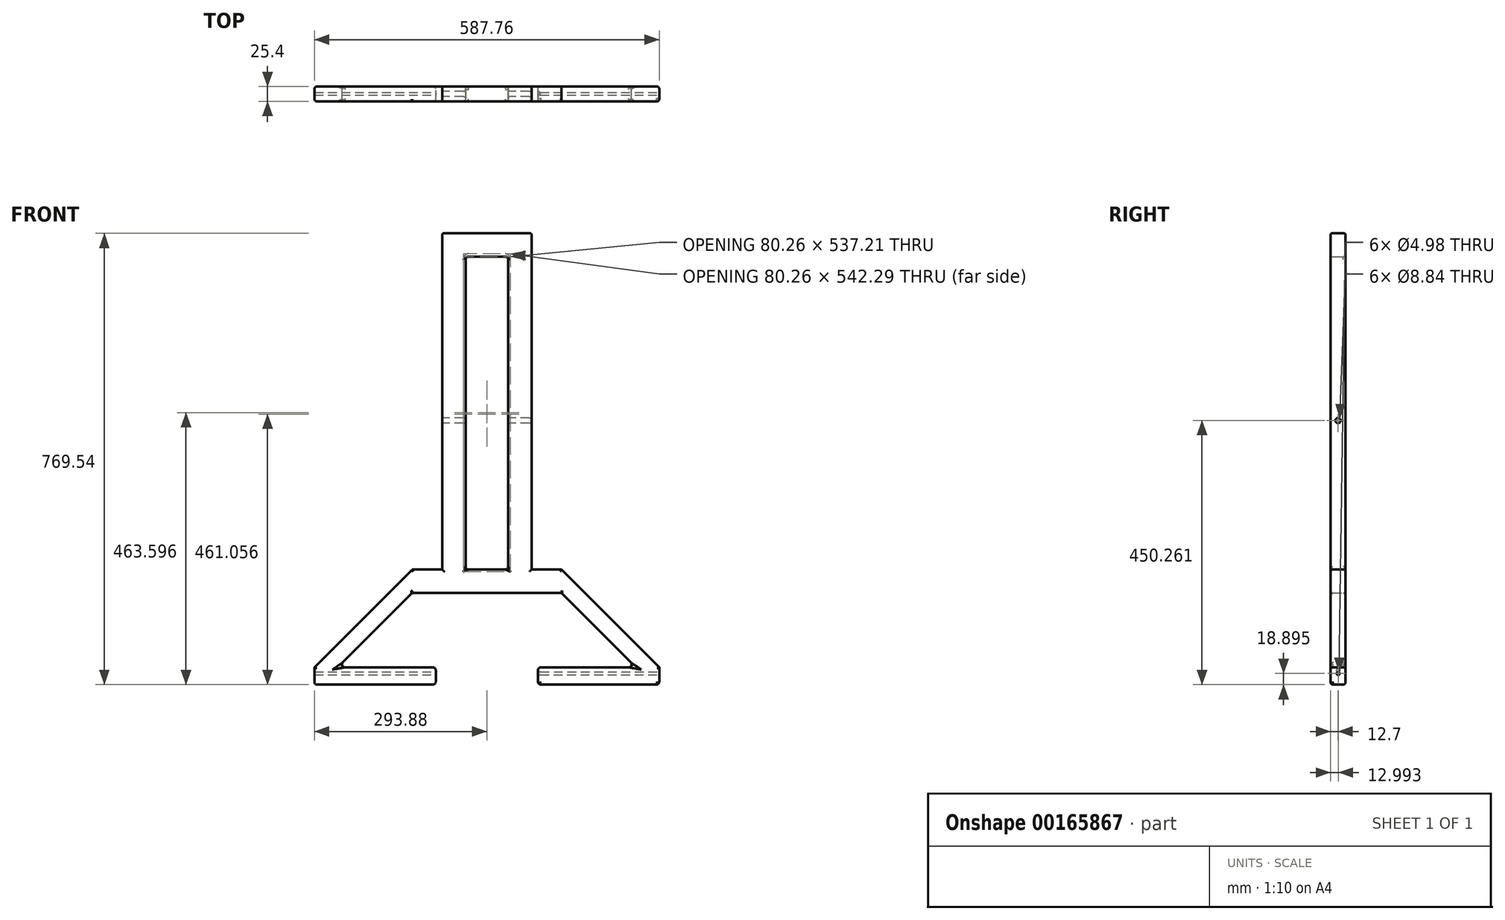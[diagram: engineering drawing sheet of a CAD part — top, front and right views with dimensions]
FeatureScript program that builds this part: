
annotation { "Feature Type Name" : "Feature", "Feature Type Description" : "" }
export const myFeature = defineFeature(function(context is Context, id is Id, definition is map)
    precondition{}
    {
        {
            var Q0;
            Q0=qCreatedBy(makeId("Front.planeOp"),FACE);
            var sketch = newSketch(context, id + "F0", { "sketchPlane" : qUnion([Q0])});
            skLineSegment(sketch, "E0.bottom", {"start": v(76.2, 19.94) * mm, "end": v(-76.2, 19.94) * mm});
            skLineSegment(sketch, "E0.top", {"start": v(76.2, -19.94) * mm, "end": v(-76.2, -19.94) * mm});
            skLineSegment(sketch, "E0.left", {"start": v(76.2, 19.94) * mm, "end": v(76.2, -19.94) * mm});
            skLineSegment(sketch, "E0.right", {"start": v(-76.2, 19.94) * mm, "end": v(-76.2, -19.94) * mm});
            skPoint(sketch, "E0.middle", {"position": v(0, 0) * mm});
            skLineSegment(sketch, "E1", {"start": v(-76.2, 19.94) * mm, "end": v(-36.32, 19.94) * mm});
            skLineSegment(sketch, "E2", {"start": v(-36.32, 19.94) * mm, "end": v(-36.32, -19.94) * mm});
            skLineSegment(sketch, "E3.MirrorCS", {"start": v(36.32, 19.94) * mm, "end": v(36.32, -19.94) * mm});
            skLineSegment(sketch, "E4", {"start": v(-76.2, -19.94) * mm, "end": v(-76.2, -553.34) * mm});
            skLineSegment(sketch, "E5", {"start": v(-36.32, -19.94) * mm, "end": v(-36.32, -553.34) * mm});
            skLineSegment(sketch, "E6", {"start": v(0, 0) * mm, "end": v(0, -73.17) * mm});
            skPoint(sketch, "E6.endSnap0", {"position": v(0, -19.94) * mm});
            skLineSegment(sketch, "E7.MirrorCS", {"start": v(36.32, -19.94) * mm, "end": v(36.32, -553.34) * mm});
            skLineSegment(sketch, "E8.MirrorCS", {"start": v(76.2, -19.94) * mm, "end": v(76.2, -553.34) * mm});
            skLineSegment(sketch, "E9", {"start": v(76.2, -553.34) * mm, "end": v(36.32, -553.34) * mm});
            skLineSegment(sketch, "E10", {"start": v(-36.32, -553.34) * mm, "end": v(-76.2, -553.34) * mm});
            skLineSegment(sketch, "E11", {"start": v(76.2, -553.34) * mm, "end": v(127, -553.34) * mm});
            skLineSegment(sketch, "E12", {"start": v(127, -553.34) * mm, "end": v(127, -593.22) * mm});
            skLineSegment(sketch, "E13", {"start": v(-76.2, -553.34) * mm, "end": v(-127, -553.34) * mm});
            skLineSegment(sketch, "E14", {"start": v(-127, -553.34) * mm, "end": v(-127, -593.22) * mm});
            skLineSegment(sketch, "E15", {"start": v(-127, -593.22) * mm, "end": v(127, -593.22) * mm});
            skLineSegment(sketch, "E16", {"start": v(36.32, -553.34) * mm, "end": v(-36.32, -553.34) * mm});
            skLineSegment(sketch, "E17", {"start": v(-127, -593.22) * mm, "end": v(-87.12, -593.22) * mm});
            skLineSegment(sketch, "E18", {"start": v(127, -593.22) * mm, "end": v(87.12, -593.22) * mm});
            skLineSegment(sketch, "E19", {"start": v(-127, -593.22) * mm, "end": v(-127, -720.22) * mm});
            skLineSegment(sketch, "E20", {"start": v(-87.12, -593.22) * mm, "end": v(-87.12, -720.22) * mm});
            skLineSegment(sketch, "E21", {"start": v(127, -593.22) * mm, "end": v(127, -720.22) * mm});
            skLineSegment(sketch, "E22", {"start": v(87.12, -593.22) * mm, "end": v(87.12, -720.22) * mm});
            skLineSegment(sketch, "E23", {"start": v(-127, -720.22) * mm, "end": v(-87.12, -720.22) * mm});
            skLineSegment(sketch, "E24", {"start": v(87.12, -720.22) * mm, "end": v(127, -720.22) * mm});
            skLineSegment(sketch, "E25", {"start": v(-127, -720.22) * mm, "end": v(-254, -720.22) * mm});
            skLineSegment(sketch, "E26", {"start": v(127, -720.22) * mm, "end": v(254, -720.22) * mm});
            skLineSegment(sketch, "E27", {"start": v(-127, -593.22) * mm, "end": v(-254, -720.22) * mm});
            skPoint(sketch, "E28.startSnap0", {"position": v(0, -593.22) * mm});
            skLineSegment(sketch, "E29.MirrorCS", {"start": v(127, -593.22) * mm, "end": v(254, -720.22) * mm});
            skLineSegment(sketch, "E30", {"start": v(-254, -720.22) * mm, "end": v(-293.88, -720.22) * mm});
            skLineSegment(sketch, "E31", {"start": v(-127, -553.34) * mm, "end": v(-293.88, -720.22) * mm});
            skLineSegment(sketch, "E32.MirrorCS", {"start": v(254, -720.22) * mm, "end": v(293.88, -720.22) * mm});
            skLineSegment(sketch, "E33.MirrorCS", {"start": v(127, -553.34) * mm, "end": v(293.88, -720.22) * mm});
            skLineSegment(sketch, "E34", {"start": v(-293.88, -720.22) * mm, "end": v(-293.88, -749.6) * mm});
            skLineSegment(sketch, "E35", {"start": v(-293.88, -749.6) * mm, "end": v(-87.12, -749.6) * mm});
            skLineSegment(sketch, "E36", {"start": v(-87.12, -720.22) * mm, "end": v(-87.12, -749.6) * mm});
            skLineSegment(sketch, "E37.MirrorCS", {"start": v(293.88, -720.22) * mm, "end": v(293.88, -749.6) * mm});
            skLineSegment(sketch, "E38.MirrorCS", {"start": v(293.88, -749.6) * mm, "end": v(87.12, -749.6) * mm});
            skLineSegment(sketch, "E39.MirrorCS", {"start": v(87.12, -720.22) * mm, "end": v(87.12, -749.6) * mm});
            skSolve(sketch);
        }
        {
            var Q0;
            {var subQ0=sQuery(id+"F0.wireOp",EDGE,"E0.left");Q0=makeQuery(id+"F0.imprint","IMPRINT",FACE,{"disambiguationData":[TD([[makeQuery(id+"F0.imprint","IMPRINT",EDGE,{"derivedFrom":subQ0}),-1.0]])]});}
            var Q1;
            {var subQ0=sQuery(id+"F0.wireOp",EDGE,"E0.right");Q1=makeQuery(id+"F0.imprint","IMPRINT",FACE,{"disambiguationData":[TD([[makeQuery(id+"F0.imprint","IMPRINT",EDGE,{"derivedFrom":subQ0}),1.0]])]});}
            var Q2;
            {var subQ0=sQuery(id+"F0.wireOp",EDGE,"E2");Q2=makeQuery(id+"F0.imprint","IMPRINT",FACE,{"disambiguationData":[TD([[makeQuery(id+"F0.imprint","IMPRINT",EDGE,{"derivedFrom":subQ0}),1.0]])]});}
            var Q3;
            Q3=makeQuery(id+"F0.imprint","IMPRINT",FACE,{"disambiguationData":[TD([[makeQuery(id+"F0.imprint","IMPRINT",EDGE,{"derivedFrom":sQuery(id+"F0.wireOp",EDGE,"E12")}),1.0]])]});
            var Q4;
            Q4=makeQuery(id+"F0.imprint","IMPRINT",FACE,{"disambiguationData":[TD([[makeQuery(id+"F0.imprint","IMPRINT",EDGE,{"derivedFrom":sQuery(id+"F0.wireOp",EDGE,"E14")}),-1.0]])]});
            var Q5;
            Q5=makeQuery(id+"F0.imprint","IMPRINT",FACE,{"disambiguationData":[TD([[makeQuery(id+"F0.imprint","IMPRINT",EDGE,{"derivedFrom":sQuery(id+"F0.wireOp",EDGE,"E17")}),-1.0]])]});
            var Q6;
            Q6=makeQuery(id+"F0.imprint","IMPRINT",FACE,{"disambiguationData":[TD([[makeQuery(id+"F0.imprint","IMPRINT",EDGE,{"derivedFrom":sQuery(id+"F0.wireOp",EDGE,"E18")}),1.0]])]});
            var Q7;
            Q7=makeQuery(id+"F0.imprint","IMPRINT",FACE,{"disambiguationData":[TD([[makeQuery(id+"F0.imprint","IMPRINT",EDGE,{"derivedFrom":sQuery(id+"F0.wireOp",EDGE,"E23")}),-1.0]])]});
            var Q8;
            Q8=makeQuery(id+"F0.imprint","IMPRINT",FACE,{"disambiguationData":[TD([[makeQuery(id+"F0.imprint","IMPRINT",EDGE,{"derivedFrom":sQuery(id+"F0.wireOp",EDGE,"E9")}),1.0]])]});
            var Q9;
            Q9=makeQuery(id+"F0.imprint","IMPRINT",FACE,{"disambiguationData":[TD([[makeQuery(id+"F0.imprint","IMPRINT",EDGE,{"derivedFrom":sQuery(id+"F0.wireOp",EDGE,"E24")}),-1.0]])]});
            var Q10;
            {var subQ2=sQuery(id+"F0.wireOp",EDGE,"E7.MirrorCS");Q10=makeQuery(id+"F0.imprint","IMPRINT",FACE,{"disambiguationData":[TD([[makeQuery(id+"F0.imprint","IMPRINT",EDGE,{"derivedFrom":subQ2}),1.0]])]});}
            var Q11;
            {var subQ0=sQuery(id+"F0.wireOp",EDGE,"E4");Q11=makeQuery(id+"F0.imprint","IMPRINT",FACE,{"disambiguationData":[TD([[makeQuery(id+"F0.imprint","IMPRINT",EDGE,{"derivedFrom":subQ0}),1.0]])]});}
            extrude(context, id + "F1", {"entities" : qUnion([Q0, Q1, Q2, Q3, Q4, Q5, Q6, Q7, Q8, Q9, Q10, Q11]), "depth" : 25.4 * mm});
        }
        {
            var Q0;
            Q0=makeQuery(id+"F1.opExtrude","CAP_EDGE",EDGE,{"disambiguationData":[OSD([sQuery(id+"F0.wireOp",EDGE,"E0.right"),sQuery(id+"F0.wireOp",EDGE,"E4")])],"isStart":false});
            var Q1;
            Q1=makeQuery(id+"F1.opExtrude","CAP_EDGE",EDGE,{"disambiguationData":[OSD([sQuery(id+"F0.wireOp",EDGE,"E13")])],"isStart":false});
            var Q2;
            Q2=makeQuery(id+"F1.opExtrude","CAP_EDGE",EDGE,{"disambiguationData":[OSD([sQuery(id+"F0.wireOp",EDGE,"E34")])],"isStart":false});
            var Q3;
            Q3=makeQuery(id+"F1.opExtrude","CAP_EDGE",EDGE,{"disambiguationData":[OSD([sQuery(id+"F0.wireOp",EDGE,"E35")])],"isStart":false});
            var Q4;
            Q4=makeQuery(id+"F1.opExtrude","CAP_EDGE",EDGE,{"disambiguationData":[OSD([sQuery(id+"F0.wireOp",EDGE,"E20"),sQuery(id+"F0.wireOp",EDGE,"E36")])],"isStart":false});
            var Q5;
            Q5=makeQuery(id+"F1.opExtrude","CAP_EDGE",EDGE,{"disambiguationData":[OSD([sQuery(id+"F0.wireOp",EDGE,"E31")])],"isStart":false});
            var Q6;
            Q6=makeQuery(id+"F1.opExtrude","CAP_EDGE",EDGE,{"disambiguationData":[OSD([sQuery(id+"F0.wireOp",EDGE,"E21")])],"isStart":false});
            var Q7;
            Q7=makeQuery(id+"F1.opExtrude","CAP_EDGE",EDGE,{"disambiguationData":[OSD([sQuery(id+"F0.wireOp",EDGE,"E29.MirrorCS")])],"isStart":false});
            var Q8;
            Q8=makeQuery(id+"F1.opExtrude","CAP_EDGE",EDGE,{"disambiguationData":[OSD([sQuery(id+"F0.wireOp",EDGE,"E26")])],"isStart":false});
            var Q9;
            Q9=makeQuery(id+"F1.opExtrude","CAP_EDGE",EDGE,{"disambiguationData":[OSD([sQuery(id+"F0.wireOp",EDGE,"E19")])],"isStart":false});
            var Q10;
            Q10=makeQuery(id+"F1.opExtrude","CAP_EDGE",EDGE,{"disambiguationData":[OSD([sQuery(id+"F0.wireOp",EDGE,"E27")])],"isStart":false});
            var Q11;
            Q11=makeQuery(id+"F1.opExtrude","CAP_EDGE",EDGE,{"disambiguationData":[OSD([sQuery(id+"F0.wireOp",EDGE,"E25")])],"isStart":false});
            var Q12;
            Q12=makeQuery(id+"F1.opExtrude","CAP_EDGE",EDGE,{"disambiguationData":[OSD([sQuery(id+"F0.wireOp",EDGE,"E33.MirrorCS")])],"isStart":false});
            var Q13;
            Q13=makeQuery(id+"F1.opExtrude","CAP_EDGE",EDGE,{"disambiguationData":[OSD([sQuery(id+"F0.wireOp",EDGE,"E11")])],"isStart":false});
            var Q14;
            Q14=makeQuery(id+"F1.opExtrude","CAP_EDGE",EDGE,{"disambiguationData":[OSD([sQuery(id+"F0.wireOp",EDGE,"E0.left"),sQuery(id+"F0.wireOp",EDGE,"E8.MirrorCS")])],"isStart":false});
            var Q15;
            Q15=makeQuery(id+"F1.opExtrude","CAP_EDGE",EDGE,{"disambiguationData":[OSD([sQuery(id+"F0.wireOp",EDGE,"E37.MirrorCS")])],"isStart":false});
            var Q16;
            Q16=makeQuery(id+"F1.opExtrude","CAP_EDGE",EDGE,{"disambiguationData":[OSD([sQuery(id+"F0.wireOp",EDGE,"E22"),sQuery(id+"F0.wireOp",EDGE,"E39.MirrorCS")])],"isStart":false});
            var Q17;
            Q17=makeQuery(id+"F1.opExtrude","CAP_EDGE",EDGE,{"disambiguationData":[OSD([sQuery(id+"F0.wireOp",EDGE,"E15")])],"isStart":false});
            var Q18;
            Q18=makeQuery(id+"F1.opExtrude","CAP_EDGE",EDGE,{"disambiguationData":[OSD([sQuery(id+"F0.wireOp",EDGE,"E7.MirrorCS")])],"isStart":false});
            var Q19;
            Q19=makeQuery(id+"F1.opExtrude","CAP_EDGE",EDGE,{"disambiguationData":[OSD([sQuery(id+"F0.wireOp",EDGE,"E5")])],"isStart":false});
            var Q20;
            Q20=makeQuery(id+"F1.opExtrude","CAP_EDGE",EDGE,{"disambiguationData":[OSD([sQuery(id+"F0.wireOp",EDGE,"E16")])],"isStart":false});
            fillet(context, id + "F2", {"entities" : qUnion([Q0, Q1, Q2, Q3, Q4, Q5, Q6, Q7, Q8, Q9, Q10, Q11, Q12, Q13, Q14, Q15, Q16, Q17, Q18, Q19, Q20]), "radius" : 3.8 * mm, "tangentPropagation" : true, "allowEdgeOverflow" : false});
        }
        {
            var Q0;
            Q0=makeQuery(id+"F1.opExtrude","CAP_EDGE",EDGE,{"disambiguationData":[OSD([sQuery(id+"F0.wireOp",EDGE,"E0.left"),sQuery(id+"F0.wireOp",EDGE,"E8.MirrorCS")])],"isStart":true});
            var Q1;
            Q1=makeQuery(id+"F1.opExtrude","CAP_EDGE",EDGE,{"disambiguationData":[OSD([sQuery(id+"F0.wireOp",EDGE,"E7.MirrorCS")])],"isStart":true});
            var Q2;
            Q2=makeQuery(id+"F1.opExtrude","CAP_EDGE",EDGE,{"disambiguationData":[OSD([sQuery(id+"F0.wireOp",EDGE,"E16")])],"isStart":true});
            var Q3;
            Q3=makeQuery(id+"F1.opExtrude","CAP_EDGE",EDGE,{"disambiguationData":[OSD([sQuery(id+"F0.wireOp",EDGE,"E5")])],"isStart":true});
            var Q4;
            Q4=makeQuery(id+"F1.opExtrude","CAP_EDGE",EDGE,{"disambiguationData":[OSD([sQuery(id+"F0.wireOp",EDGE,"E0.right"),sQuery(id+"F0.wireOp",EDGE,"E4")])],"isStart":true});
            var Q5;
            Q5=makeQuery(id+"F1.opExtrude","CAP_EDGE",EDGE,{"disambiguationData":[OSD([sQuery(id+"F0.wireOp",EDGE,"E13")])],"isStart":true});
            var Q6;
            Q6=makeQuery(id+"F1.opExtrude","SWEPT_EDGE",EDGE,{"disambiguationData":[OSD([sQuery(id+"F0.wireOp",EDGE,"E13"),sQuery(id+"F0.wireOp",EDGE,"E14"),sQuery(id+"F0.wireOp",EDGE,"E31")])]});
            var Q7;
            Q7=makeQuery(id+"F1.opExtrude","CAP_EDGE",EDGE,{"disambiguationData":[OSD([sQuery(id+"F0.wireOp",EDGE,"E31")])],"isStart":true});
            var Q8;
            Q8=makeQuery(id+"F1.opExtrude","CAP_EDGE",EDGE,{"disambiguationData":[OSD([sQuery(id+"F0.wireOp",EDGE,"E11")])],"isStart":true});
            var Q9;
            Q9=makeQuery(id+"F1.opExtrude","CAP_EDGE",EDGE,{"disambiguationData":[OSD([sQuery(id+"F0.wireOp",EDGE,"E33.MirrorCS")])],"isStart":true});
            var Q10;
            Q10=makeQuery(id+"F1.opExtrude","CAP_EDGE",EDGE,{"disambiguationData":[OSD([sQuery(id+"F0.wireOp",EDGE,"E37.MirrorCS")])],"isStart":true});
            var Q11;
            Q11=makeQuery(id+"F1.opExtrude","CAP_EDGE",EDGE,{"disambiguationData":[OSD([sQuery(id+"F0.wireOp",EDGE,"E22"),sQuery(id+"F0.wireOp",EDGE,"E39.MirrorCS")])],"isStart":true});
            var Q12;
            Q12=makeQuery(id+"F1.opExtrude","CAP_EDGE",EDGE,{"disambiguationData":[OSD([sQuery(id+"F0.wireOp",EDGE,"E20"),sQuery(id+"F0.wireOp",EDGE,"E36")])],"isStart":true});
            var Q13;
            Q13=makeQuery(id+"F1.opExtrude","CAP_EDGE",EDGE,{"disambiguationData":[OSD([sQuery(id+"F0.wireOp",EDGE,"E34")])],"isStart":true});
            var Q14;
            Q14=makeQuery(id+"F1.opExtrude","SWEPT_EDGE",EDGE,{"disambiguationData":[OSD([sQuery(id+"F0.wireOp",EDGE,"E34"),sQuery(id+"F0.wireOp",EDGE,"E35")])]});
            var Q15;
            Q15=makeQuery(id+"F1.opExtrude","CAP_EDGE",EDGE,{"disambiguationData":[OSD([sQuery(id+"F0.wireOp",EDGE,"E35")])],"isStart":true});
            var Q16;
            Q16=makeQuery(id+"F1.opExtrude","CAP_EDGE",EDGE,{"disambiguationData":[OSD([sQuery(id+"F0.wireOp",EDGE,"E38.MirrorCS")])],"isStart":true});
            var Q17;
            Q17=makeQuery(id+"F1.opExtrude","CAP_EDGE",EDGE,{"disambiguationData":[OSD([sQuery(id+"F0.wireOp",EDGE,"E29.MirrorCS")])],"isStart":true});
            var Q18;
            Q18=makeQuery(id+"F1.opExtrude","CAP_EDGE",EDGE,{"disambiguationData":[OSD([sQuery(id+"F0.wireOp",EDGE,"E26")])],"isStart":true});
            var Q19;
            Q19=makeQuery(id+"F1.opExtrude","CAP_EDGE",EDGE,{"disambiguationData":[OSD([sQuery(id+"F0.wireOp",EDGE,"E25")])],"isStart":true});
            var Q20;
            Q20=makeQuery(id+"F1.opExtrude","CAP_EDGE",EDGE,{"disambiguationData":[OSD([sQuery(id+"F0.wireOp",EDGE,"E19")])],"isStart":true});
            var Q21;
            Q21=makeQuery(id+"F1.opExtrude","CAP_EDGE",EDGE,{"disambiguationData":[OSD([sQuery(id+"F0.wireOp",EDGE,"E21")])],"isStart":true});
            var Q22;
            Q22=makeQuery(id+"F1.opExtrude","CAP_EDGE",EDGE,{"disambiguationData":[OSD([sQuery(id+"F0.wireOp",EDGE,"E27")])],"isStart":true});
            fillet(context, id + "F3", {"entities" : qUnion([Q0, Q1, Q2, Q3, Q4, Q5, Q6, Q7, Q8, Q9, Q10, Q11, Q12, Q13, Q14, Q15, Q16, Q17, Q18, Q19, Q20, Q21, Q22]), "radius" : 3.8 * mm, "tangentPropagation" : true, "allowEdgeOverflow" : false});
        }
        {
            var Q0;
            Q0=makeQuery(id+"F1.opExtrude","CAP_EDGE",EDGE,{"disambiguationData":[OSD([sQuery(id+"F0.wireOp",EDGE,"E0.top")])],"isStart":true});
            var Q1;
            Q1=makeQuery(id+"F1.opExtrude","SWEPT_EDGE",EDGE,{"disambiguationData":[OSD([sQuery(id+"F0.wireOp",EDGE,"E0.top"),sQuery(id+"F0.wireOp",EDGE,"E2"),sQuery(id+"F0.wireOp",EDGE,"E5")])]});
            var Q2;
            Q2=makeQuery(id+"F1.opExtrude","SWEPT_EDGE",EDGE,{"disambiguationData":[OSD([sQuery(id+"F0.wireOp",EDGE,"E15"),sQuery(id+"F0.wireOp",EDGE,"E17"),sQuery(id+"F0.wireOp",EDGE,"E20")])]});
            var Q3;
            Q3=makeQuery(id+"F1.opExtrude","SWEPT_EDGE",EDGE,{"disambiguationData":[OSD([sQuery(id+"F0.wireOp",EDGE,"E38.MirrorCS"),sQuery(id+"F0.wireOp",EDGE,"E39.MirrorCS")])]});
            var Q4;
            Q4=makeQuery(id+"F1.opExtrude","SWEPT_EDGE",EDGE,{"disambiguationData":[OSD([sQuery(id+"F0.wireOp",EDGE,"E35"),sQuery(id+"F0.wireOp",EDGE,"E36")])]});
            var Q5;
            Q5=makeQuery(id+"F1.opExtrude","SWEPT_EDGE",EDGE,{"disambiguationData":[OSD([sQuery(id+"F0.wireOp",EDGE,"E15"),sQuery(id+"F0.wireOp",EDGE,"E18"),sQuery(id+"F0.wireOp",EDGE,"E22")])]});
            var Q6;
            Q6=makeQuery(id+"F1.opExtrude","SWEPT_EDGE",EDGE,{"disambiguationData":[OSD([sQuery(id+"F0.wireOp",EDGE,"E0.top"),sQuery(id+"F0.wireOp",EDGE,"E3.MirrorCS"),sQuery(id+"F0.wireOp",EDGE,"E7.MirrorCS")])]});
            var Q7;
            Q7=makeQuery(id+"F1.opExtrude","SWEPT_EDGE",EDGE,{"disambiguationData":[OSD([sQuery(id+"F0.wireOp",EDGE,"E7.MirrorCS"),sQuery(id+"F0.wireOp",EDGE,"E9"),sQuery(id+"F0.wireOp",EDGE,"E16")])]});
            var Q8;
            Q8=makeQuery(id+"F1.opExtrude","SWEPT_EDGE",EDGE,{"disambiguationData":[OSD([sQuery(id+"F0.wireOp",EDGE,"E5"),sQuery(id+"F0.wireOp",EDGE,"E10"),sQuery(id+"F0.wireOp",EDGE,"E16")])]});
            var Q9;
            Q9=makeQuery(id+"F1.opExtrude","SWEPT_EDGE",EDGE,{"disambiguationData":[OSD([sQuery(id+"F0.wireOp",EDGE,"E25"),sQuery(id+"F0.wireOp",EDGE,"E27"),sQuery(id+"F0.wireOp",EDGE,"E30")])]});
            var Q10;
            Q10=makeQuery(id+"F1.opExtrude","SWEPT_EDGE",EDGE,{"disambiguationData":[OSD([sQuery(id+"F0.wireOp",EDGE,"E14"),sQuery(id+"F0.wireOp",EDGE,"E17"),sQuery(id+"F0.wireOp",EDGE,"E19"),sQuery(id+"F0.wireOp",EDGE,"E27")])]});
            var Q11;
            Q11=makeQuery(id+"F1.opExtrude","SWEPT_EDGE",EDGE,{"disambiguationData":[OSD([sQuery(id+"F0.wireOp",EDGE,"E12"),sQuery(id+"F0.wireOp",EDGE,"E18"),sQuery(id+"F0.wireOp",EDGE,"E21"),sQuery(id+"F0.wireOp",EDGE,"E29.MirrorCS")])]});
            var Q12;
            Q12=makeQuery(id+"F1.opExtrude","SWEPT_EDGE",EDGE,{"disambiguationData":[OSD([sQuery(id+"F0.wireOp",EDGE,"E21"),sQuery(id+"F0.wireOp",EDGE,"E24"),sQuery(id+"F0.wireOp",EDGE,"E26")])]});
            var Q13;
            Q13=makeQuery(id+"F1.opExtrude","SWEPT_EDGE",EDGE,{"disambiguationData":[OSD([sQuery(id+"F0.wireOp",EDGE,"E26"),sQuery(id+"F0.wireOp",EDGE,"E29.MirrorCS"),sQuery(id+"F0.wireOp",EDGE,"E32.MirrorCS")])]});
            fillet(context, id + "F4", {"entities" : qUnion([Q0, Q1, Q2, Q3, Q4, Q5, Q6, Q7, Q8, Q9, Q10, Q11, Q12, Q13]), "radius" : 5.08 * mm, "tangentPropagation" : true, "allowEdgeOverflow" : false});
        }
        {
            var Q0;
            Q0=makeQuery(id+"F1.opExtrude","SWEPT_FACE",FACE,{"disambiguationData":[OSD([sQuery(id+"F0.wireOp",EDGE,"E37.MirrorCS")])]});
            var sketch = newSketch(context, id + "F5", { "sketchPlane" : qUnion([Q0])});
            skPoint(sketch, "E40.middle", {"position": v(-12.4, -730.7) * mm});
            skCircle(sketch, "E41", {"center": v(-12.4, -730.7) * mm, "radius": 2.49 * mm});
            skSolve(sketch);
        }
        {
            var Q0;
            Q0=makeQuery(id+"F5.imprint","IMPRINT",FACE,{"disambiguationData":[TD([[makeQuery(id+"F5.imprint","IMPRINT",EDGE,{"derivedFrom":sQuery(id+"F5.wireOp",EDGE,"E41")}),1.0]])]});
            extrude(context, id + "F6", {"entities" : qUnion([Q0]), "operationType" : NewBodyOperationType.REMOVE, "endBound" : BoundingType.THROUGH_ALL, "oppositeDirection" : true, "depth" : 25.4 * mm});
        }
        {
            var Q0;
            Q0=makeQuery(id+"F6.boolean.opBoolean","COPY",EDGE,{"derivedFrom":makeQuery(id+"F6.opExtrude","CAP_EDGE",EDGE,{"disambiguationData":[OSD([sQuery(id+"F5.wireOp",EDGE,"E41")])],"isStart":true})});
            var Q1;
            Q1=makeQuery(id+"F6.boolean.opBoolean","INTERSECT",EDGE,{"derivedFrom":[makeQuery(id+"F1.opExtrude","SWEPT_FACE",FACE,{"disambiguationData":[OSD([sQuery(id+"F0.wireOp",EDGE,"E22"),sQuery(id+"F0.wireOp",EDGE,"E39.MirrorCS")])]}),makeQuery(id+"F6.opExtrude","SWEPT_FACE",FACE,{"disambiguationData":[OSD([sQuery(id+"F5.wireOp",EDGE,"E41")])]})]});
            fillet(context, id + "F7", {"entities" : qUnion([Q0, Q1]), "radius" : 3.8 * mm, "tangentPropagation" : true, "allowEdgeOverflow" : false});
        }
        {
            var Q0;
            Q0=makeQuery(id+"F1.opExtrude","SWEPT_FACE",FACE,{"disambiguationData":[OSD([sQuery(id+"F0.wireOp",EDGE,"E0.right"),sQuery(id+"F0.wireOp",EDGE,"E4")])]});
            var sketch = newSketch(context, id + "F8", { "sketchPlane" : qUnion([Q0])});
            skCircle(sketch, "E42", {"center": v(12.7, -299.34) * mm, "radius": 4.42 * mm});
            skSolve(sketch);
        }
        {
            var Q0;
            Q0=makeQuery(id+"F8.imprint","IMPRINT",FACE,{"disambiguationData":[TD([[makeQuery(id+"F8.imprint","IMPRINT",EDGE,{"derivedFrom":sQuery(id+"F8.wireOp",EDGE,"E42")}),1.0]])]});
            extrude(context, id + "F9", {"entities" : qUnion([Q0]), "operationType" : NewBodyOperationType.REMOVE, "endBound" : BoundingType.THROUGH_ALL, "oppositeDirection" : true, "depth" : 25.4 * mm});
        }
        {
            var Q0;
            Q0=makeQuery(id+"F9.boolean.opBoolean","COPY",EDGE,{"derivedFrom":makeQuery(id+"F9.opExtrude","CAP_EDGE",EDGE,{"disambiguationData":[OSD([sQuery(id+"F8.wireOp",EDGE,"E42")])],"isStart":true})});
            var Q1;
            Q1=makeQuery(id+"F9.boolean.opBoolean","INTERSECT",EDGE,{"derivedFrom":[makeQuery(id+"F1.opExtrude","SWEPT_FACE",FACE,{"disambiguationData":[OSD([sQuery(id+"F0.wireOp",EDGE,"E7.MirrorCS")])]}),makeQuery(id+"F9.opExtrude","SWEPT_FACE",FACE,{"disambiguationData":[OSD([sQuery(id+"F8.wireOp",EDGE,"E42")])]})]});
            var Q2;
            Q2=makeQuery(id+"F9.boolean.opBoolean","INTERSECT",EDGE,{"derivedFrom":[makeQuery(id+"F1.opExtrude","SWEPT_FACE",FACE,{"disambiguationData":[OSD([sQuery(id+"F0.wireOp",EDGE,"E5")])]}),makeQuery(id+"F9.opExtrude","SWEPT_FACE",FACE,{"disambiguationData":[OSD([sQuery(id+"F8.wireOp",EDGE,"E42")])]})]});
            var Q3;
            Q3=makeQuery(id+"F9.boolean.opBoolean","INTERSECT",EDGE,{"derivedFrom":[makeQuery(id+"F1.opExtrude","SWEPT_FACE",FACE,{"disambiguationData":[OSD([sQuery(id+"F0.wireOp",EDGE,"E0.left"),sQuery(id+"F0.wireOp",EDGE,"E8.MirrorCS")])]}),makeQuery(id+"F9.opExtrude","SWEPT_FACE",FACE,{"disambiguationData":[OSD([sQuery(id+"F8.wireOp",EDGE,"E42")])]})]});
            fillet(context, id + "F10", {"entities" : qUnion([Q0, Q1, Q2, Q3]), "radius" : 3.8 * mm, "tangentPropagation" : true, "allowEdgeOverflow" : false});
        }
        {
            var Q0;
            Q0=makeQuery(id+"F1.opExtrude","SWEPT_EDGE",EDGE,{"disambiguationData":[OSD([sQuery(id+"F0.wireOp",EDGE,"E0.right"),sQuery(id+"F0.wireOp",EDGE,"E1")])]});
            fillet(context, id + "F11", {"entities" : qUnion([Q0]), "radius" : 2.54 * mm, "tangentPropagation" : true, "allowEdgeOverflow" : false});
        }
        {
            var Q0;
            Q0=makeQuery(id+"F1.opExtrude","CAP_EDGE",EDGE,{"disambiguationData":[OSD([sQuery(id+"F0.wireOp",EDGE,"E15")])],"isStart":true});
            fillet(context, id + "F12", {"entities" : qUnion([Q0]), "radius" : 3.8 * mm, "tangentPropagation" : true, "allowEdgeOverflow" : false});
        }
    });
